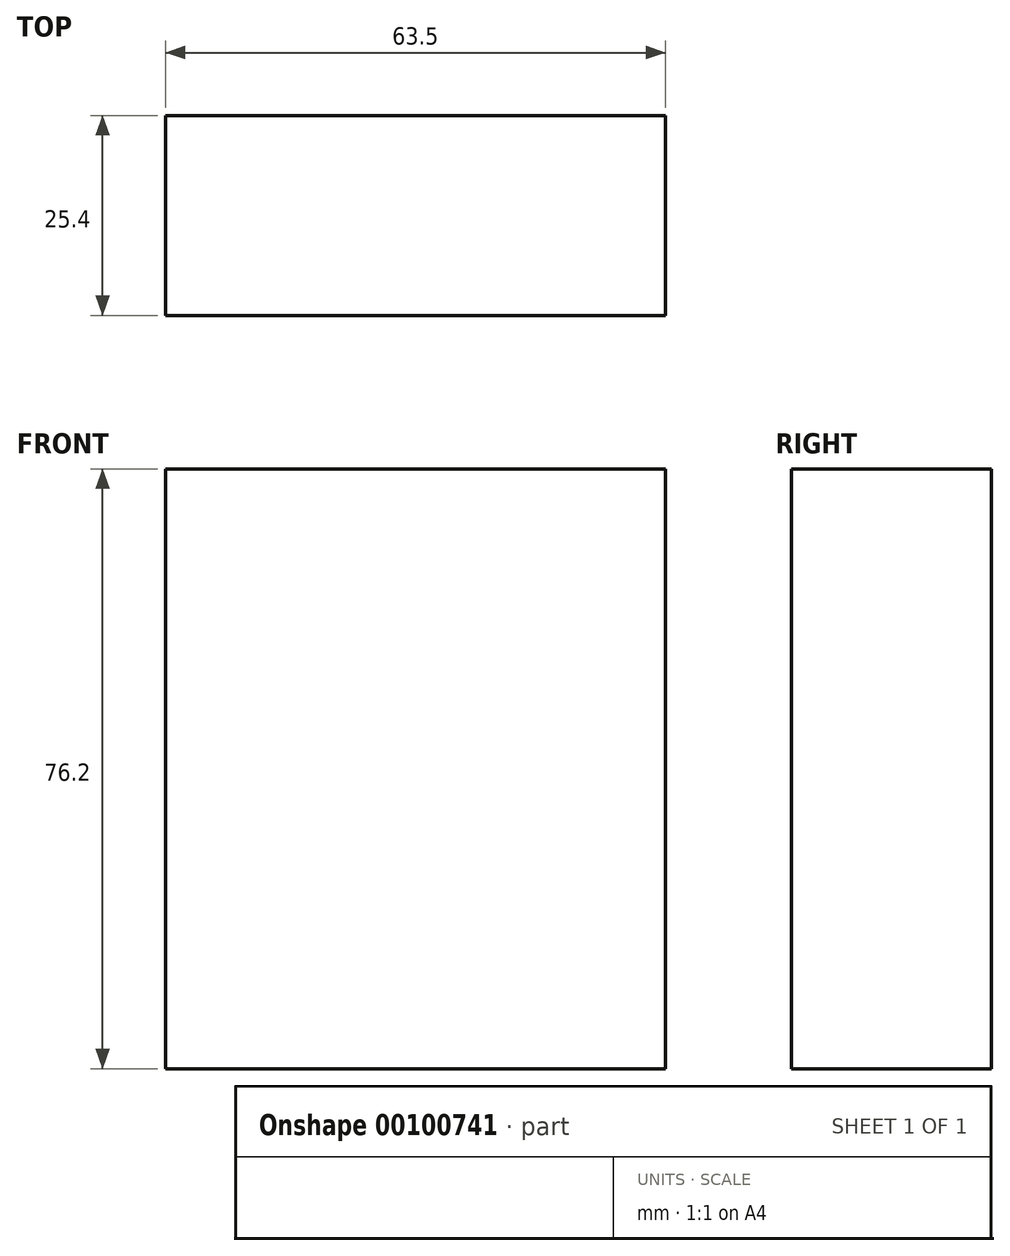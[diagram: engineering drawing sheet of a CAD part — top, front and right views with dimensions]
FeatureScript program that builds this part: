
annotation { "Feature Type Name" : "Feature", "Feature Type Description" : "" }
export const myFeature = defineFeature(function(context is Context, id is Id, definition is map)
    precondition{}
    {
        {
            var Q0;
            Q0=qCreatedBy(makeId("Front.planeOp"),FACE);
            var sketch = newSketch(context, id + "F0", { "sketchPlane" : qUnion([Q0])});
            skLineSegment(sketch, "E0.bottom", {"start": v(0, 0) * mm, "end": v(63.5, 0) * mm});
            skLineSegment(sketch, "E0.top", {"start": v(0, 76.2) * mm, "end": v(63.5, 76.2) * mm});
            skLineSegment(sketch, "E0.left", {"start": v(0, 0) * mm, "end": v(0, 76.2) * mm});
            skLineSegment(sketch, "E0.right", {"start": v(63.5, 0) * mm, "end": v(63.5, 76.2) * mm});
            skSolve(sketch);
        }
        {
            var Q0;
            Q0=makeQuery(id+"F0.imprint","IMPRINT",FACE,{"disambiguationData":[TD([[makeQuery(id+"F0.imprint","IMPRINT",EDGE,{"derivedFrom":sQuery(id+"F0.wireOp",EDGE,"E0.bottom")}),1.0]])]});
            extrude(context, id + "F1", {"entities" : qUnion([Q0]), "depth" : 25.4 * mm});
        }
    });
